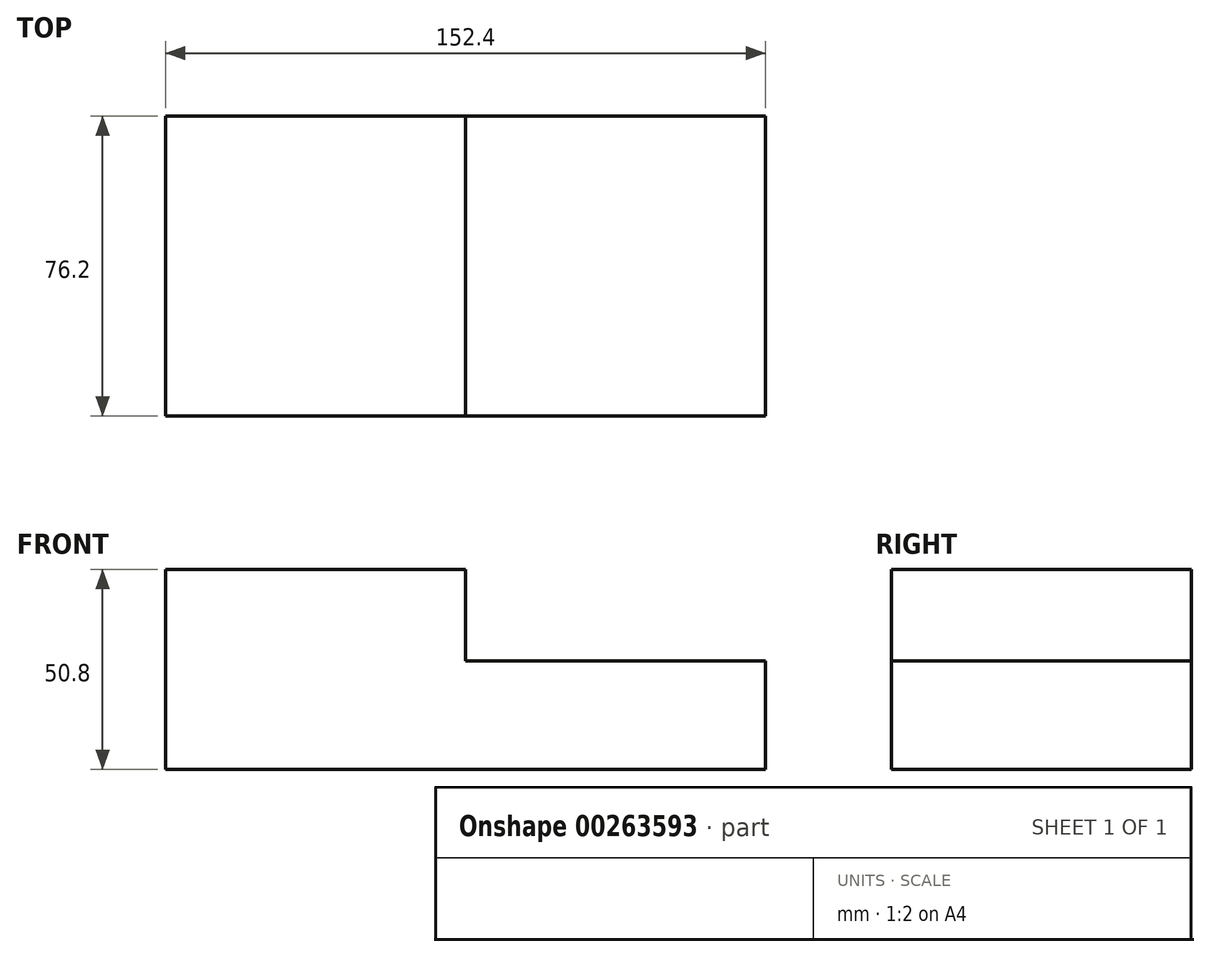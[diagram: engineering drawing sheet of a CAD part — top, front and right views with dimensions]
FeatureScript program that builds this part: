
annotation { "Feature Type Name" : "Feature", "Feature Type Description" : "" }
export const myFeature = defineFeature(function(context is Context, id is Id, definition is map)
    precondition{}
    {
        {
            var Q0;
            Q0=qCreatedBy(makeId("Front.planeOp"),FACE);
            var sketch = newSketch(context, id + "F0", { "sketchPlane" : qUnion([Q0])});
            skLineSegment(sketch, "E0", {"start": v(0, 0) * mm, "end": v(0, 50.8) * mm});
            skLineSegment(sketch, "E1", {"start": v(0, 50.8) * mm, "end": v(76.2, 50.8) * mm});
            skLineSegment(sketch, "E2", {"start": v(76.2, 50.8) * mm, "end": v(76.2, 27.63) * mm});
            skLineSegment(sketch, "E3", {"start": v(0, 0) * mm, "end": v(152.4, 0) * mm});
            skLineSegment(sketch, "E4", {"start": v(76.2, 27.63) * mm, "end": v(152.4, 27.63) * mm});
            skLineSegment(sketch, "E5", {"start": v(152.4, 27.63) * mm, "end": v(152.4, 0) * mm});
            skSolve(sketch);
        }
        {
            var Q0;
            Q0 = qSketchRegion(id + "F0", true);
            extrude(context, id + "F1", {"entities" : qUnion([Q0]), "depth" : 76.2 * mm});
        }
    });
